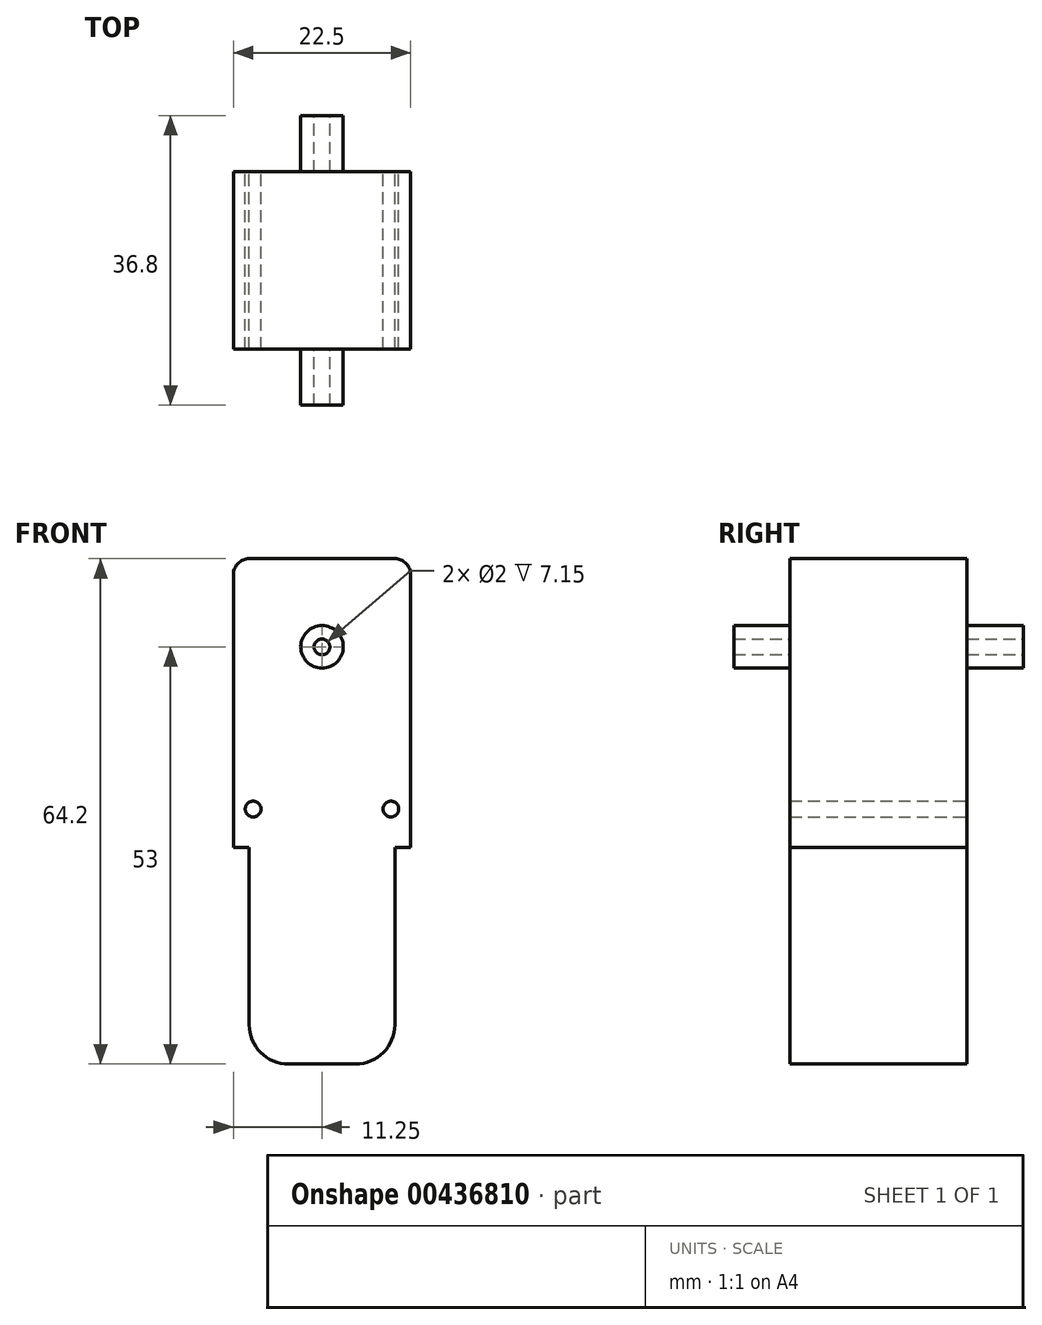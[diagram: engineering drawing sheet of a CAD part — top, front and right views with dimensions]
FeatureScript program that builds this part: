
annotation { "Feature Type Name" : "Feature", "Feature Type Description" : "" }
export const myFeature = defineFeature(function(context is Context, id is Id, definition is map)
    precondition{}
    {
        {
            var Q0;
            Q0=qCreatedBy(makeId("Front.planeOp"),FACE);
            var sketch = newSketch(context, id + "F0", { "sketchPlane" : qUnion([Q0])});
            skLineSegment(sketch, "E0.bottom", {"start": v(9.25, 32.1) * mm, "end": v(-9.25, 32.1) * mm});
            skLineSegment(sketch, "E0.top", {"start": v(4.25, -32.1) * mm, "end": v(-4.25, -32.1) * mm});
            skLineSegment(sketch, "E0.left", {"start": v(11.25, 30.1) * mm, "end": v(11.25, -4.59) * mm});
            skLineSegment(sketch, "E0.right", {"start": v(-11.25, 30.1) * mm, "end": v(-11.25, -4.59) * mm});
            skPoint(sketch, "E0.middle", {"position": v(0, 0) * mm});
            skPoint(sketch, "E1.visualSharp", {"position": v(11.25, 32.1) * mm});
            skArc(sketch, "E1.filletArc", {"start": v(11.25, 30.1) * mm, "mid": v(10.66, 31.51) * mm, "end": v(9.25, 32.1) * mm});
            skPoint(sketch, "E2.visualSharp", {"position": v(-11.25, 32.1) * mm});
            skArc(sketch, "E2.filletArc", {"start": v(-9.25, 32.1) * mm, "mid": v(-10.66, 31.51) * mm, "end": v(-11.25, 30.1) * mm});
            skCircle(sketch, "E3", {"center": v(8.75, 0.3) * mm, "radius": 1 * mm});
            skCircle(sketch, "E4", {"center": v(-8.75, 0.3) * mm, "radius": 1 * mm});
            skLineSegment(sketch, "E5", {"start": v(-11.25, -4.59) * mm, "end": v(11.25, -4.59) * mm});
            skLineSegment(sketch, "E6.0", {"start": v(-9.25, -4.59) * mm, "end": v(-9.25, -27.1) * mm});
            skLineSegment(sketch, "E7.0", {"start": v(9.25, -4.59) * mm, "end": v(9.25, -27.1) * mm});
            skPoint(sketch, "E8.orphan", {"position": v(11.25, -32.1) * mm});
            skPoint(sketch, "E9.orphan", {"position": v(-11.25, -32.1) * mm});
            skPoint(sketch, "E10.visualSharp", {"position": v(-9.25, -32.1) * mm});
            skPoint(sketch, "E11.visualSharp", {"position": v(9.25, -32.1) * mm});
            skArc(sketch, "E12.filletArc", {"start": v(-9.25, -27.1) * mm, "mid": v(-7.79, -30.64) * mm, "end": v(-4.25, -32.1) * mm});
            skArc(sketch, "E13.filletArc", {"start": v(4.25, -32.1) * mm, "mid": v(7.79, -30.64) * mm, "end": v(9.25, -27.1) * mm});
            skSolve(sketch);
        }
        {
            var Q0;
            Q0 = qSketchRegion(id + "F0", true);
            extrude(context, id + "F1", {"entities" : qUnion([Q0]), "depth" : 22.5 * mm, "symmetric" : true});
        }
        {
            var Q0;
            Q0=qCreatedBy(makeId("Front.planeOp"),FACE);
            var sketch = newSketch(context, id + "F2", { "sketchPlane" : qUnion([Q0])});
            skCircle(sketch, "E14", {"center": v(0, 20.9) * mm, "radius": 2.7 * mm});
            skCircle(sketch, "E15", {"center": v(0, 20.9) * mm, "radius": 1 * mm});
            skSolve(sketch);
        }
        {
            var Q0;
            Q0 = qSketchRegion(id + "F2", true);
            extrude(context, id + "F3", {"entities" : qUnion([Q0]), "operationType" : NewBodyOperationType.ADD, "depth" : 36.8 * mm, "symmetric" : true});
        }
    });
